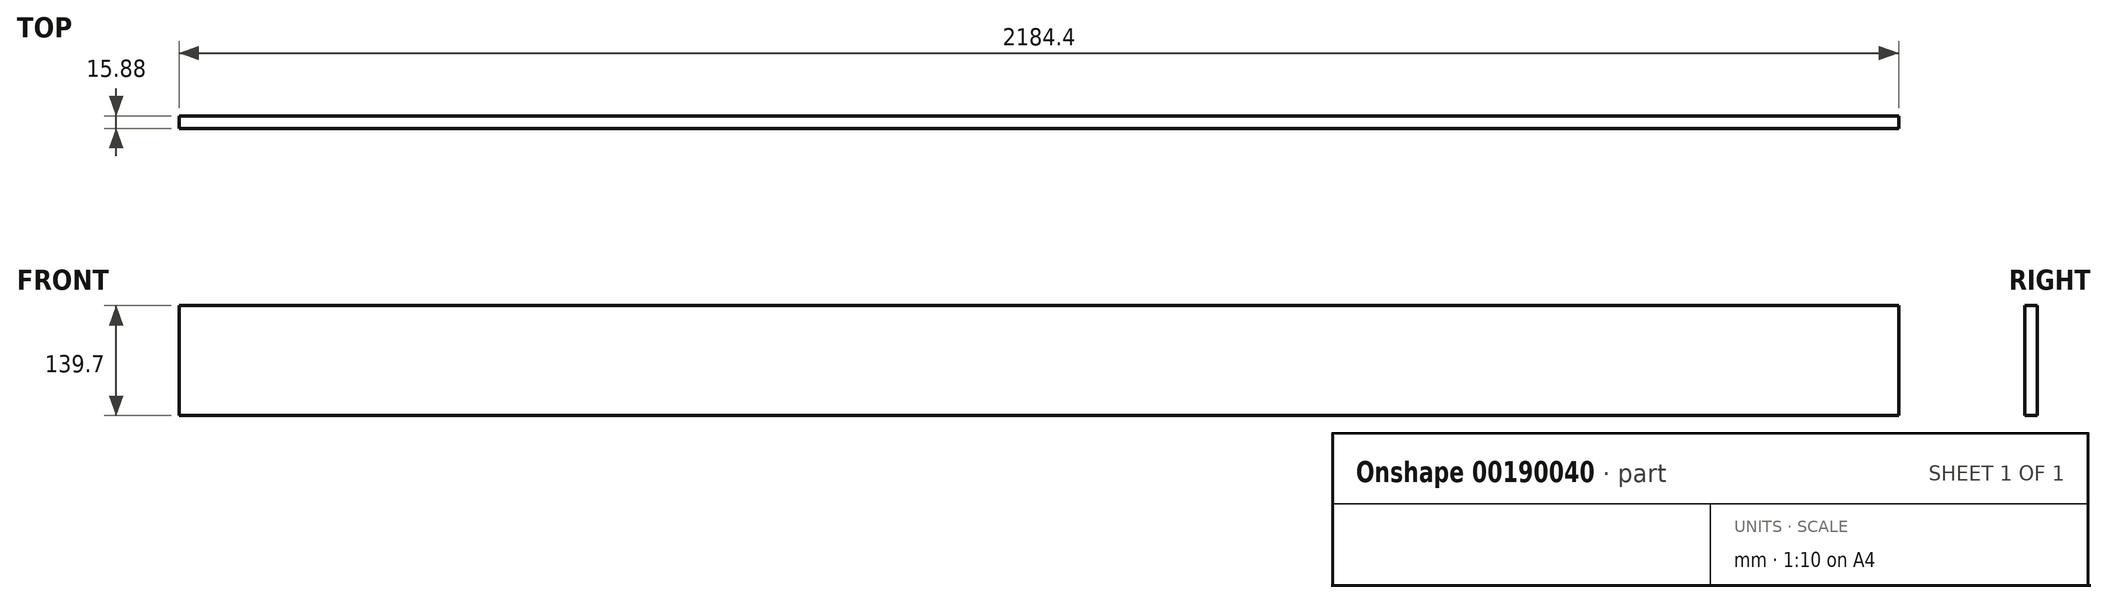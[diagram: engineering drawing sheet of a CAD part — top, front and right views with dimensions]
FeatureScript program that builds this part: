
annotation { "Feature Type Name" : "Feature", "Feature Type Description" : "" }
export const myFeature = defineFeature(function(context is Context, id is Id, definition is map)
    precondition{}
    {
        {
            var Q0;
            Q0=qCreatedBy(makeId("Front.planeOp"),FACE);
            var sketch = newSketch(context, id + "F0", { "sketchPlane" : qUnion([Q0])});
            skLineSegment(sketch, "E0.bottom", {"start": v(1092.2, 69.85) * mm, "end": v(-1092.2, 69.85) * mm});
            skLineSegment(sketch, "E0.top", {"start": v(1092.2, -69.85) * mm, "end": v(-1092.2, -69.85) * mm});
            skLineSegment(sketch, "E0.left", {"start": v(1092.2, 69.85) * mm, "end": v(1092.2, -69.85) * mm});
            skLineSegment(sketch, "E0.right", {"start": v(-1092.2, 69.85) * mm, "end": v(-1092.2, -69.85) * mm});
            skPoint(sketch, "E0.middle", {"position": v(0, 0) * mm});
            skSolve(sketch);
        }
        {
            var Q0;
            Q0 = qSketchRegion(id + "F0", true);
            extrude(context, id + "F1", {"entities" : qUnion([Q0]), "depth" : 15.88 * mm});
        }
    });
